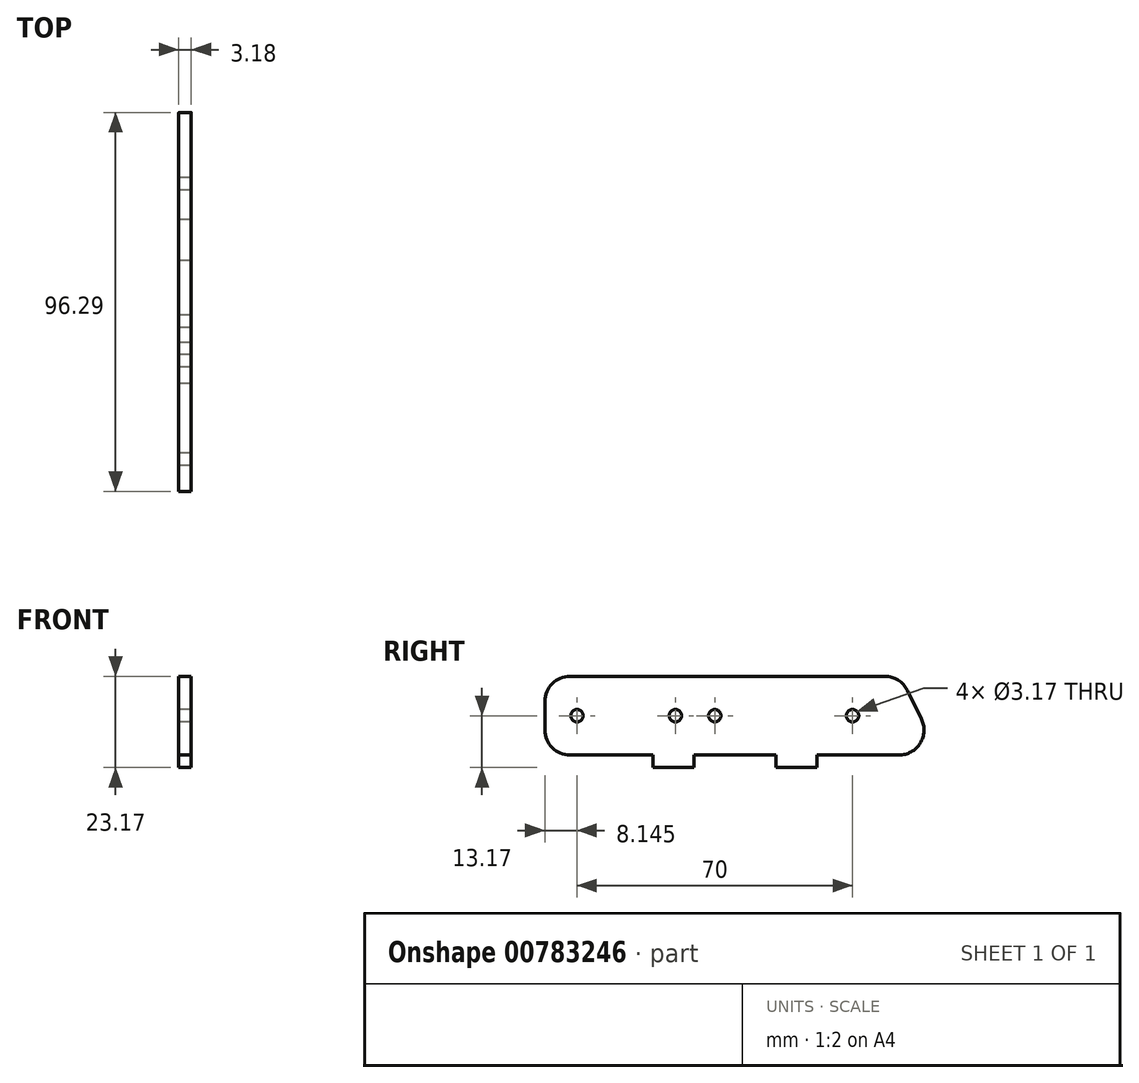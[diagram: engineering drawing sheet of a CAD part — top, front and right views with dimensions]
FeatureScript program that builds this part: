
annotation { "Feature Type Name" : "Feature", "Feature Type Description" : "" }
export const myFeature = defineFeature(function(context is Context, id is Id, definition is map)
    precondition{}
    {
        {
            var Q0;
            Q0=qCreatedBy(makeId("Right.planeOp"),FACE);
            var sketch = newSketch(context, id + "F0", { "sketchPlane" : qUnion([Q0])});
            skLineSegment(sketch, "E0", {"start": v(-32.28, 0) * mm, "end": v(-32.03, 0) * mm});
            skArc(sketch, "E1.filletArc", {"start": v(-38.63, 6.35) * mm, "mid": v(-36.77, 1.86) * mm, "end": v(-32.28, 0) * mm});
            skArc(sketch, "E2.filletArc", {"start": v(51.3, 0) * mm, "mid": v(56.7, 2.98) * mm, "end": v(57.02, 9.13) * mm});
            skArc(sketch, "E3.filletArc", {"start": v(53.46, 16.43) * mm, "mid": v(51.12, 19.03) * mm, "end": v(47.75, 20) * mm});
            skLineSegment(sketch, "E4", {"start": v(53.46, 16.43) * mm, "end": v(57.02, 9.13) * mm});
            skLineSegment(sketch, "E5", {"start": v(-28.72, 20) * mm, "end": v(47.75, 20) * mm});
            skLineSegment(sketch, "E6.top", {"start": v(-11.2, -3.17) * mm, "end": v(-0.78, -3.17) * mm});
            skLineSegment(sketch, "E6.left", {"start": v(-11.2, 0) * mm, "end": v(-11.2, -3.17) * mm});
            skLineSegment(sketch, "E6.right", {"start": v(30.47, 0) * mm, "end": v(30.47, -3.17) * mm});
            skLineSegment(sketch, "E7", {"start": v(20.05, 0) * mm, "end": v(20.05, -3.17) * mm});
            skLineSegment(sketch, "E8", {"start": v(-0.78, 0) * mm, "end": v(-0.78, -3.17) * mm});
            skLineSegment(sketch, "E9.trimOffspring", {"start": v(20.05, -3.17) * mm, "end": v(30.47, -3.17) * mm});
            skLineSegment(sketch, "E10", {"start": v(-32.03, 0) * mm, "end": v(-11.2, 0) * mm});
            skLineSegment(sketch, "E11.trimOffspring", {"start": v(30.47, 0) * mm, "end": v(51.3, 0) * mm});
            skLineSegment(sketch, "E12.trimOffspring", {"start": v(-0.78, 0) * mm, "end": v(20.05, 0) * mm});
            skPoint(sketch, "E13.end.orphan", {"position": v(39.52, 10) * mm});
            skCircle(sketch, "E14", {"center": v(4.52, 10) * mm, "radius": 1.59 * mm});
            skCircle(sketch, "E15", {"center": v(39.52, 10) * mm, "radius": 1.59 * mm});
            skLineSegment(sketch, "E16.top", {"start": v(-32.28, 20) * mm, "end": v(-28.72, 20) * mm});
            skLineSegment(sketch, "E16.left", {"start": v(-38.63, 6.35) * mm, "end": v(-38.63, 13.65) * mm});
            skArc(sketch, "E17.filletArc", {"start": v(-32.28, 20) * mm, "mid": v(-36.77, 18.14) * mm, "end": v(-38.63, 13.65) * mm});
            skCircle(sketch, "E18", {"center": v(-30.48, 10) * mm, "radius": 1.59 * mm});
            skCircle(sketch, "E19", {"center": v(-5.48, 10) * mm, "radius": 1.59 * mm});
            skSolve(sketch);
        }
        {
            var Q0;
            Q0=qSketchRegion(id+"F0",true);
            extrude(context, id + "F1", {"entities" : qUnion([Q0]), "depth" : 3.17 * mm, "offsetDistance" : 25.4 * mm});
        }
    });
